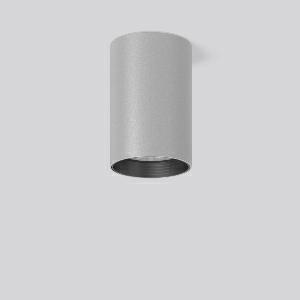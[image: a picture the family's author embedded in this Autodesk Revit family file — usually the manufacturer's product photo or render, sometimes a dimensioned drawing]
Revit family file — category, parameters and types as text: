
# Revit family: heledon_maxi_a_931229_004_1_76_de53
name_source: partatom
category: Lighting Fixtures
units: mm (PartAtom-declared; Revit-internal decimal feet)

## family parameters
Cut with Voids When Loaded = No
Host = Face
Light Source = No
Part Type = Normal
Room Calculation Point = No
Round Connector Dimension = Use Diameter
Shared = No

## types (1)
- HELEDON maxi A (1 x LED Modul 940, 3800 lm, 4000)
    Apparent Load = 35 VA
    Approval mark = CE
    CIE Flux Codes = 96 100 100 100 100
    Color Rendering = 92
    Color Temperature = 4000
    Default Elevation = 1800 mm
    Description = Series: HELEDON maxi
Cylindrical surface-mounted downlight. Housing: die-cast aluminium, powder-coated. Internal ceiling frame polycarbonate with bayonet mounting. Black plastic ring and recessed LED to prevent glare from the side. Optical assembly with lens made of plastic (polycarbonate) for the best homogeneous light distribution - can be changed without tools. Best colour rendering index Ra>90. Suitable for Ceiling mounting. Easy installation with a separate ceiling frame with bayonet mounting and plug connection. Driver integrated. Connected via plug-in connector. High quality converter without flickering and stroboscopic effect. The following accessories can be mounted without use of tools: interchangeable lenses, decorative glasses, honeycomb louvre, clear and frosted diffusers, white interchangeable plastic ring. 
Colour: silver
Diameter: 123 mm
Height: 183 mm
Lamp: LED
Socket: without socket
Colour temperature: 4000K
Colour rendering index (CRI): 92
System power: 35 W
Rated luminous flux: 3800 lm
Luminous efficiency: 109 lm/W
Control gear: Converter, dimmable, DALI
Protection class: I
Type of protection: IP 20
    Height = 183 mm
    Lamp = 1 x LED Modul 940
    Lamp Light Flux = 3800 lm
    Lamp count = 1
    Length = 123 mm
    Lifetime = 50000 h
    Luminous efficacy = 109 lm/W
    Manufacturer = RZB
    ModVariant = No
    Model = 931229.004.1.76
    Mounting Place = Ceiling
    Mounting Type = Surface mounted
    Number of Poles = 1
    OnlyDefault = Yes
    Power Factor = 1
    Product Name = HELEDON maxi A
    Product group = Surface mounted downlights
    ProductGroupID = 302
    Protection Class = Protection class I
    Protection Degree = IP 20
    RLX_Detail_Level = 1
    RLX_Emergency_Light_Flux = 0 lm
    RLX_Emergency_Type = 0
    RLX_Emergency_Type_DB = No
    RlxData = <blob elided: 100373 chars, md5=dbc9bc7a>
    Socket = socket
    Standby Power = 0 W
    System Light Flux = 3800 lm
    System Power = 35 W
    Type Comments = Product without accessories
    Type Image = 931193.004.jpg
    URL = http://relux.com
    VarID = ---
    Voltage = 230 V
    Voltage Range = 220-240 V
    Weight = 0.00 kg
    Width = 0 mm  [stored 0 ft]

note: [stored X ft] marks values corroborated as IEEE doubles in the binary element streams (Revit-internal decimal feet)

## geometry (parser evidence)
native form markers: Blend x4, Sweep x9
no freeform markers — native parametric forms only
